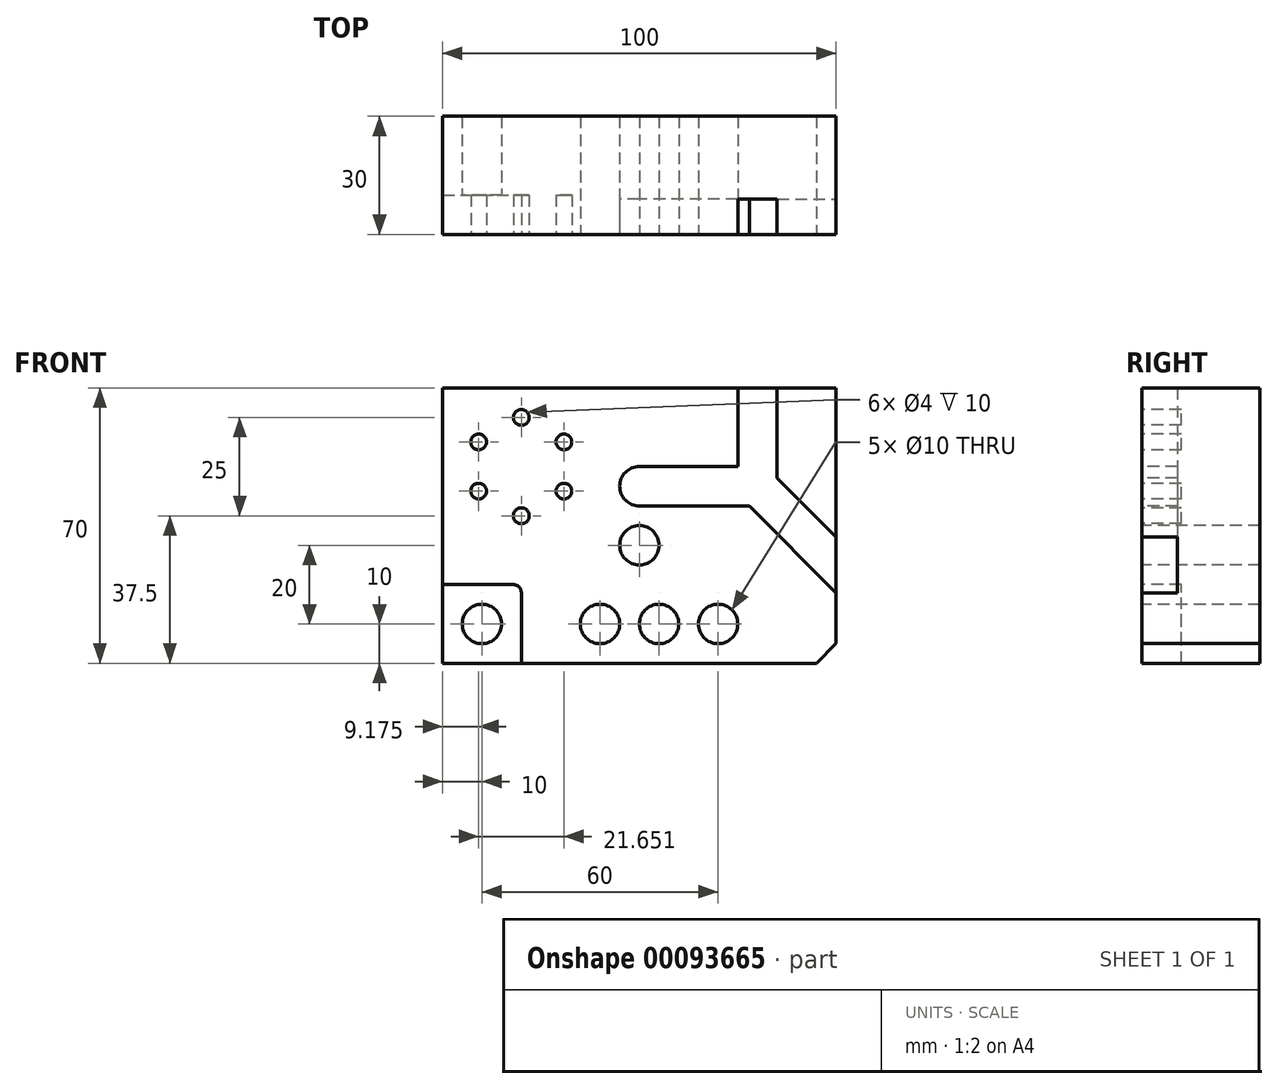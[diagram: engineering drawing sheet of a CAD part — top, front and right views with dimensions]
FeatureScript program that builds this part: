
annotation { "Feature Type Name" : "Feature", "Feature Type Description" : "" }
export const myFeature = defineFeature(function(context is Context, id is Id, definition is map)
    precondition{}
    {
        {
            var Q0;
            Q0=qCreatedBy(makeId("Front.planeOp"),FACE);
            var sketch = newSketch(context, id + "F0", { "sketchPlane" : qUnion([Q0])});
            skLineSegment(sketch, "E0.bottom", {"start": v(0, 0) * mm, "end": v(100, 0) * mm});
            skLineSegment(sketch, "E0.top", {"start": v(0, 70) * mm, "end": v(100, 70) * mm});
            skLineSegment(sketch, "E0.left", {"start": v(0, 0) * mm, "end": v(0, 70) * mm});
            skLineSegment(sketch, "E0.right", {"start": v(100, 0) * mm, "end": v(100, 70) * mm});
            skSolve(sketch);
        }
        {
            var Q0;
            Q0=makeQuery(id+"F0.imprint","IMPRINT",FACE,{"disambiguationData":[TD([[makeQuery(id+"F0.imprint","IMPRINT",EDGE,{"derivedFrom":sQuery(id+"F0.wireOp",EDGE,"E0.bottom")}),1.0]])]});
            extrude(context, id + "F1", {"entities" : qUnion([Q0]), "depth" : 30 * mm});
        }
        {
            var Q0;
            Q0=makeQuery(id+"F1.opExtrude","CAP_FACE",FACE,{"disambiguationData":[OSD([sQuery(id+"F0.wireOp",EDGE,"E0.bottom"),sQuery(id+"F0.wireOp",EDGE,"E0.top"),sQuery(id+"F0.wireOp",EDGE,"E0.left"),sQuery(id+"F0.wireOp",EDGE,"E0.right")])],"isStart":false});
            var sketch = newSketch(context, id + "F2", { "sketchPlane" : qUnion([Q0])});
            skLineSegment(sketch, "E1.0", {"start": v(75, 70) * mm, "end": v(75, 50) * mm});
            skLineSegment(sketch, "E2.0", {"start": v(85, 70) * mm, "end": v(85, 47.07) * mm});
            skLineSegment(sketch, "E3.0", {"start": v(77.93, 40) * mm, "end": v(100, 17.93) * mm});
            skLineSegment(sketch, "E4.0", {"start": v(85, 47.07) * mm, "end": v(100, 32.07) * mm});
            skLineSegment(sketch, "E5.0", {"start": v(77.93, 40) * mm, "end": v(50, 40) * mm});
            skLineSegment(sketch, "E6.0", {"start": v(75, 50) * mm, "end": v(50, 50) * mm});
            skArc(sketch, "E7", {"start": v(50, 50) * mm, "mid": v(45, 45) * mm, "end": v(50, 40) * mm});
            skLineSegment(sketch, "E8", {"start": v(75, 70) * mm, "end": v(85, 70) * mm});
            skLineSegment(sketch, "E9", {"start": v(100, 32.07) * mm, "end": v(100, 17.93) * mm});
            skSolve(sketch);
        }
        {
            var Q0;
            Q0=makeQuery(id+"F2.imprint","IMPRINT",FACE,{"disambiguationData":[TD([[makeQuery(id+"F2.imprint","IMPRINT",EDGE,{"derivedFrom":sQuery(id+"F2.wireOp",EDGE,"E1.0")}),1.0]])]});
            extrude(context, id + "F3", {"entities" : qUnion([Q0]), "operationType" : NewBodyOperationType.REMOVE, "oppositeDirection" : true, "depth" : 9 * mm});
        }
        {
            var Q0;
            {var subQ0=sQuery(id+"F0.wireOp",EDGE,"E0.right");var subQ1=sQuery(id+"F0.wireOp",EDGE,"E0.left");var subQ2=sQuery(id+"F0.wireOp",EDGE,"E0.top");var subQ3=sQuery(id+"F0.wireOp",EDGE,"E0.bottom");Q0=makeQuery(id+"F3.boolean.opBoolean","SPLIT",FACE,{"disambiguationData":[TD([makeQuery(id+"F1.opExtrude","SWEPT_FACE",FACE,{"disambiguationData":[OSD([subQ3])]})])],"derivedFrom":makeQuery(id+"F1.opExtrude","CAP_FACE",FACE,{"disambiguationData":[OSD([subQ3,subQ2,subQ1,subQ0])],"isStart":false})});}
            var sketch = newSketch(context, id + "F4", { "sketchPlane" : qUnion([Q0])});
            skLineSegment(sketch, "E10.bottom", {"start": v(0, 0) * mm, "end": v(20, 0) * mm});
            skLineSegment(sketch, "E10.top", {"start": v(0, 20) * mm, "end": v(20, 20) * mm});
            skLineSegment(sketch, "E10.left", {"start": v(0, 0) * mm, "end": v(0, 20) * mm});
            skLineSegment(sketch, "E10.right", {"start": v(20, 0) * mm, "end": v(20, 20) * mm});
            skSolve(sketch);
        }
        {
            var Q0;
            Q0=makeQuery(id+"F4.imprint","IMPRINT",FACE,{"disambiguationData":[TD([[makeQuery(id+"F4.imprint","IMPRINT",EDGE,{"derivedFrom":sQuery(id+"F4.wireOp",EDGE,"E10.bottom")}),1.0]])]});
            extrude(context, id + "F5", {"entities" : qUnion([Q0]), "operationType" : NewBodyOperationType.REMOVE, "oppositeDirection" : true, "depth" : 10 * mm});
        }
        {
            var Q0;
            Q0=makeQuery(id+"F5.boolean.opBoolean","COPY",FACE,{"derivedFrom":makeQuery(id+"F5.opExtrude","CAP_FACE",FACE,{"disambiguationData":[OSD([sQuery(id+"F4.wireOp",EDGE,"E10.bottom"),sQuery(id+"F4.wireOp",EDGE,"E10.top"),sQuery(id+"F4.wireOp",EDGE,"E10.left"),sQuery(id+"F4.wireOp",EDGE,"E10.right")])],"isStart":false})});
            var sketch = newSketch(context, id + "F6", { "sketchPlane" : qUnion([Q0])});
            skCircle(sketch, "E11", {"center": v(10, 10) * mm, "radius": 5 * mm});
            skPoint(sketch, "E11.centerSnap0", {"position": v(0, 10) * mm});
            skPoint(sketch, "E11.centerSnap1", {"position": v(10, 20) * mm});
            skSolve(sketch);
        }
        {
            var Q0;
            Q0=makeQuery(id+"F6.imprint","IMPRINT",FACE,{"disambiguationData":[TD([[makeQuery(id+"F6.imprint","IMPRINT",EDGE,{"derivedFrom":sQuery(id+"F6.wireOp",EDGE,"E11")}),1.0]])]});
            extrude(context, id + "F7", {"entities" : qUnion([Q0]), "operationType" : NewBodyOperationType.REMOVE, "oppositeDirection" : true, "depth" : 25 * mm});
        }
        {
            var Q0;
            {var subQ0=sQuery(id+"F0.wireOp",EDGE,"E0.right");var subQ1=sQuery(id+"F0.wireOp",EDGE,"E0.left");var subQ2=sQuery(id+"F0.wireOp",EDGE,"E0.top");var subQ3=sQuery(id+"F0.wireOp",EDGE,"E0.bottom");Q0=makeQuery(id+"F3.boolean.opBoolean","SPLIT",FACE,{"disambiguationData":[TD([makeQuery(id+"F1.opExtrude","SWEPT_FACE",FACE,{"disambiguationData":[OSD([subQ3])]})])],"derivedFrom":makeQuery(id+"F1.opExtrude","CAP_FACE",FACE,{"disambiguationData":[OSD([subQ3,subQ2,subQ1,subQ0])],"isStart":false})});}
            var sketch = newSketch(context, id + "F8", { "sketchPlane" : qUnion([Q0])});
            skCircle(sketch, "E12", {"center": v(20, 50) * mm, "radius": 12.5 * mm, "construction": true});
            skCircle(sketch, "E13", {"center": v(20, 62.5) * mm, "radius": 2 * mm});
            skCircle(sketch, "E14.1.0", {"center": v(9.17, 56.25) * mm, "radius": 2 * mm});
            skCircle(sketch, "E14.2.0", {"center": v(9.17, 43.75) * mm, "radius": 2 * mm});
            skCircle(sketch, "E14.3.0", {"center": v(20, 37.5) * mm, "radius": 2 * mm});
            skCircle(sketch, "E15.1.4.0", {"center": v(30.83, 43.75) * mm, "radius": 2 * mm});
            skCircle(sketch, "E15.1.5.0", {"center": v(30.83, 56.25) * mm, "radius": 2 * mm});
            skSolve(sketch);
        }
        {
            var Q0;
            Q0 = qSketchRegion(id + "F8", true);
            extrude(context, id + "F9", {"entities" : qUnion([Q0]), "operationType" : NewBodyOperationType.REMOVE, "oppositeDirection" : true, "depth" : 10 * mm});
        }
        {
            var Q0;
            {var subQ0=sQuery(id+"F0.wireOp",EDGE,"E0.right");var subQ1=sQuery(id+"F0.wireOp",EDGE,"E0.left");var subQ2=sQuery(id+"F0.wireOp",EDGE,"E0.top");var subQ3=sQuery(id+"F0.wireOp",EDGE,"E0.bottom");Q0=makeQuery(id+"F3.boolean.opBoolean","SPLIT",FACE,{"disambiguationData":[TD([makeQuery(id+"F1.opExtrude","SWEPT_FACE",FACE,{"disambiguationData":[OSD([subQ3])]})])],"derivedFrom":makeQuery(id+"F1.opExtrude","CAP_FACE",FACE,{"disambiguationData":[OSD([subQ3,subQ2,subQ1,subQ0])],"isStart":false})});}
            var sketch = newSketch(context, id + "F10", { "sketchPlane" : qUnion([Q0])});
            skLineSegment(sketch, "E16", {"start": v(37.16, 10) * mm, "end": v(81.1, 10) * mm, "construction": true});
            skLineSegment(sketch, "E17", {"start": v(40, 15) * mm, "end": v(40, 5) * mm, "construction": true});
            skLineSegment(sketch, "E18", {"start": v(55, 14.96) * mm, "end": v(55, 5.04) * mm, "construction": true});
            skLineSegment(sketch, "E19", {"start": v(70, 14.96) * mm, "end": v(70, 5.04) * mm, "construction": true});
            skCircle(sketch, "E20", {"center": v(40, 10) * mm, "radius": 5 * mm});
            skCircle(sketch, "E21", {"center": v(55, 10) * mm, "radius": 5 * mm});
            skCircle(sketch, "E22", {"center": v(70, 10) * mm, "radius": 5 * mm});
            skCircle(sketch, "E23", {"center": v(50, 30) * mm, "radius": 5 * mm});
            skSolve(sketch);
        }
        {
            var Q0;
            Q0 = qSketchRegion(id + "F10", true);
            extrude(context, id + "F11", {"entities" : qUnion([Q0]), "operationType" : NewBodyOperationType.REMOVE, "oppositeDirection" : true, "depth" : 41.45 * mm});
        }
        {
            var Q0;
            Q0=makeQuery(id+"F1.opExtrude","SWEPT_EDGE",EDGE,{"disambiguationData":[OSD([sQuery(id+"F0.wireOp",EDGE,"E0.bottom"),sQuery(id+"F0.wireOp",EDGE,"E0.right")])]});
            chamfer(context, id + "F12", {"entities" : qUnion([Q0]), "width" : 5 * mm, "tangentPropagation" : true});
        }
        {
            var Q0;
            Q0=makeQuery(id+"F5.boolean.opBoolean","COPY",EDGE,{"derivedFrom":makeQuery(id+"F5.opExtrude","SWEPT_EDGE",EDGE,{"disambiguationData":[OSD([sQuery(id+"F4.wireOp",EDGE,"E10.top"),sQuery(id+"F4.wireOp",EDGE,"E10.right")])]})});
            fillet(context, id + "F13", {"entities" : qUnion([Q0]), "radius" : 2 * mm, "tangentPropagation" : true, "allowEdgeOverflow" : false});
        }
    });
